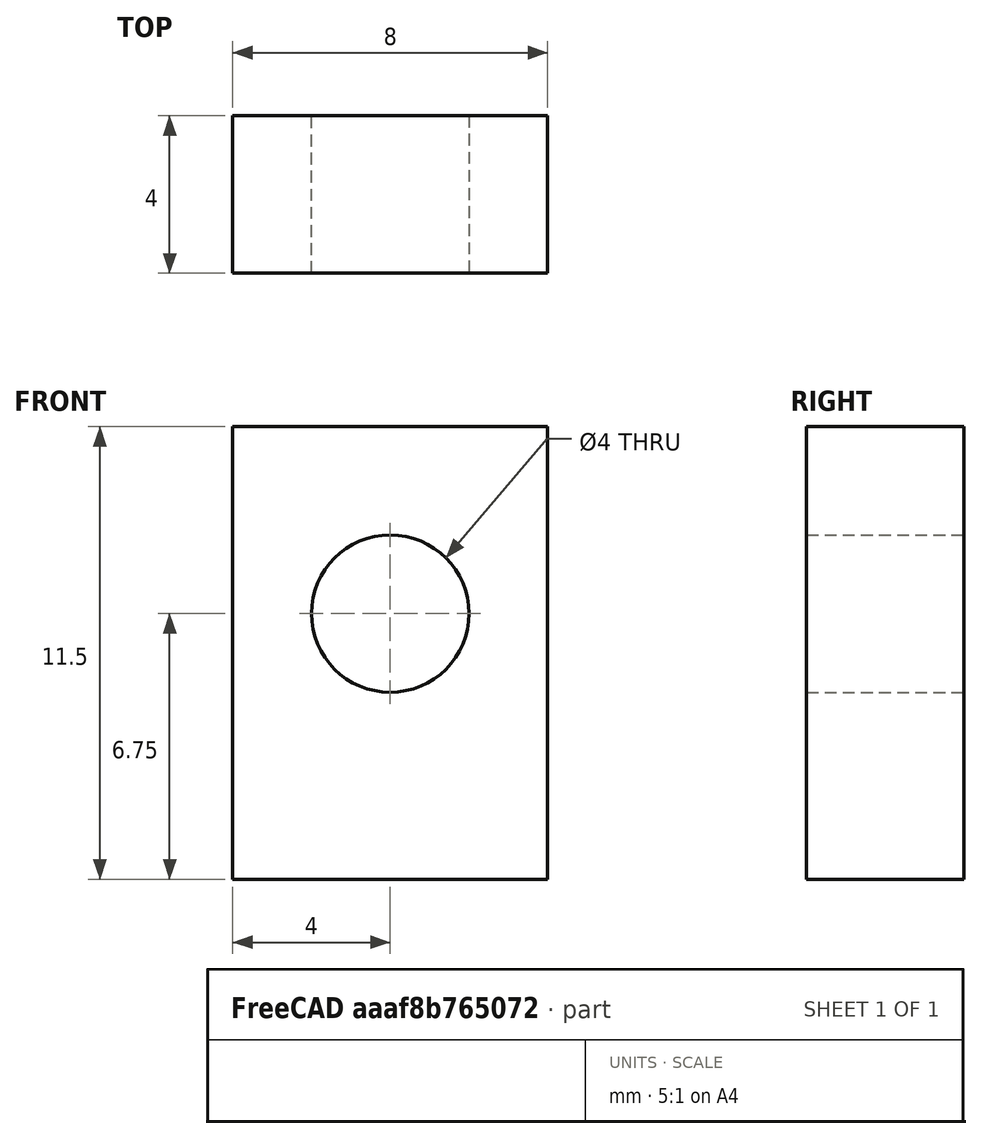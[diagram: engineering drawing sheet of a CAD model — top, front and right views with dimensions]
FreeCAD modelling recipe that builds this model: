
FCSTD DOCUMENT  (FreeCAD 0.19R24276 (Git))
Label: nub_spacer
License: All rights reserved
LicenseURL: http://en.wikipedia.org/wiki/All_rights_reserved
objects: Sketcher::SketchObject×1, PartDesign::Pad×1, PartDesign::Body×1
note: 4 computed .brp shape members not serialized (recipe doc carries the construction recipe); baked Part::Feature solids carry a one-line shape summary decoded from their .brp

FEATURE [Sketcher::SketchObject] Sketch
  FullyConstrained = true
  MapMode = 5
  Placement = pos=(0,0,0) rot=(1,0,0;1.5708rad)
  Support = -> [XZ_Plane]
  sketch-geometry (6):
    g0: LineSegment StartX=0 StartY=11.5 StartZ=0 EndX=8 EndY=11.5 EndZ=0
    g1: LineSegment StartX=8 StartY=11.5 StartZ=0 EndX=8 EndY=0 EndZ=0
    g2: LineSegment StartX=8 StartY=0 StartZ=0 EndX=0 EndY=0 EndZ=0
    g3: LineSegment StartX=0 StartY=0 StartZ=0 EndX=0 EndY=11.5 EndZ=0
    g4: Circle CenterX=4 CenterY=6.75 CenterZ=0 NormalX=0 NormalY=0 NormalZ=1 AngleXU=0 Radius=2
    g5: LineSegment StartX=4 StartY=11.5 StartZ=0 EndX=4 EndY=0 EndZ=0
  constraints (16):
    c: Coincident(g0,g1)
    c: Coincident(g1,g2)
    c: Coincident(g2,g3)
    c: Coincident(g3,g0)
    c: Horizontal(g0)
    c: Horizontal(g2)
    c: Vertical(g1)
    c: Vertical(g3)
    c: Coincident(g2,g-1)
    c: Distance(g1) = 11.5
    c: Distance(g2) = 8
    c: DistanceY(g1,g4) = 6.75
    c: Diameter(g4) = 4
    c: Symmetric(g2,g1,g5)
    c: Symmetric(g0,g0,g5)
    c: PointOnObject(g4,g5)
FEATURE [PartDesign::Pad] Pad
  Direction = (1,1,1)
  Length = 4
  Length2 = 100
  Placement = pos=(0,0,0) rot=(1,0,0;1.5708rad)
  Profile = -> Sketch
  Type = 0
FEATURE [PartDesign::Body] Body
  Group = -> [Sketch,Pad]
  Origin = -> Origin
  Tip = -> Pad
